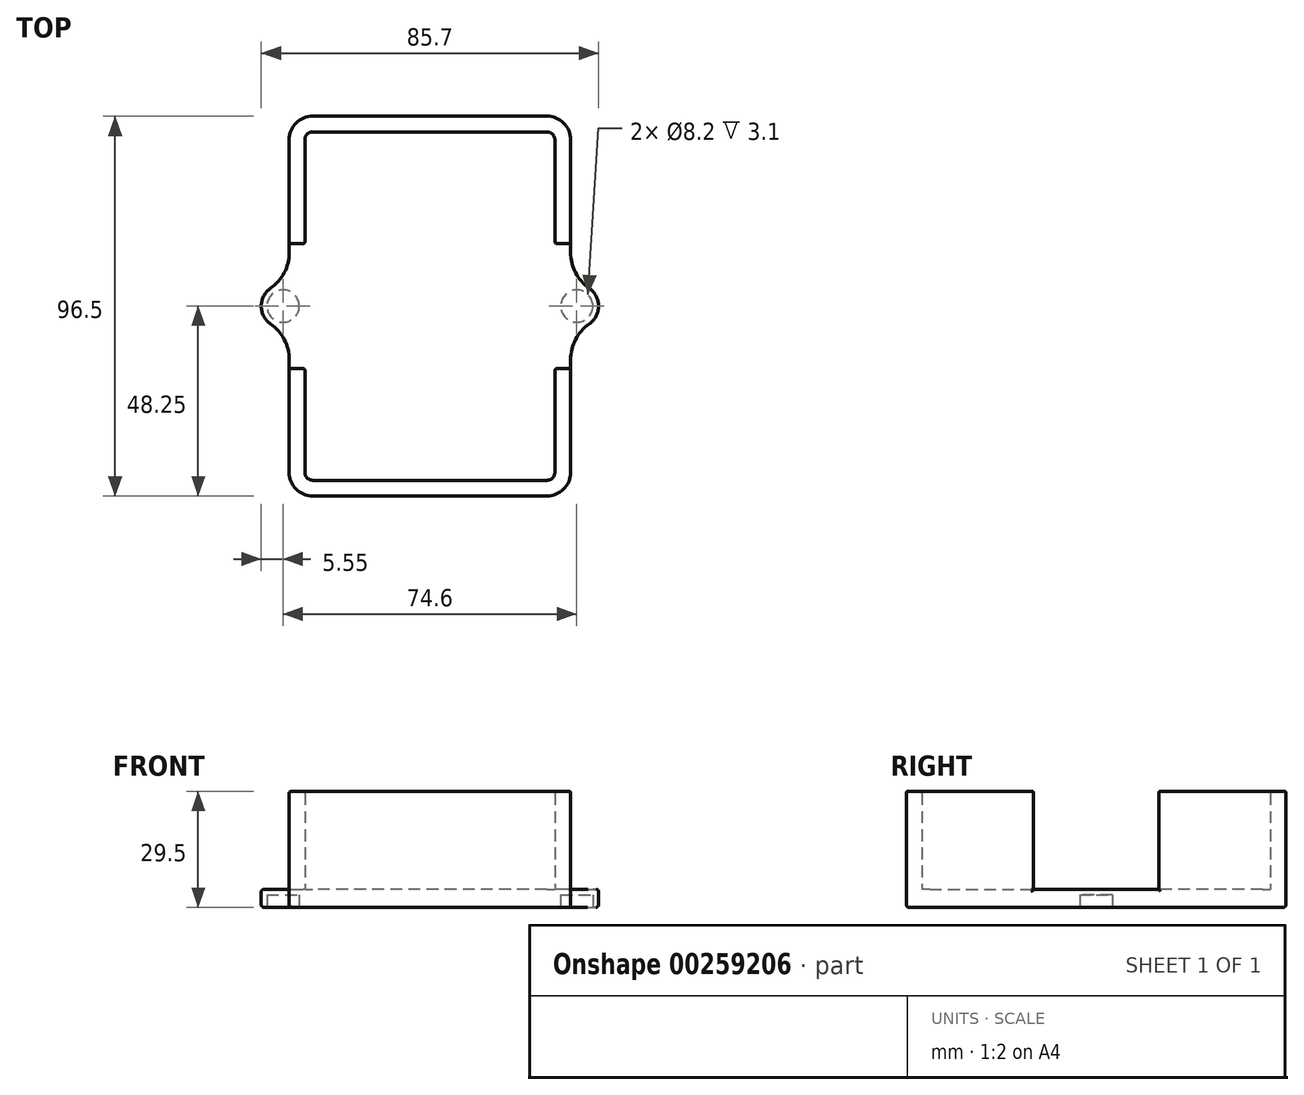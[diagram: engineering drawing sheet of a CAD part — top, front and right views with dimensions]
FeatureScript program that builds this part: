
annotation { "Feature Type Name" : "Feature", "Feature Type Description" : "" }
export const myFeature = defineFeature(function(context is Context, id is Id, definition is map)
    precondition{}
    {
        {
            var Q0;
            Q0=qCreatedBy(makeId("Top.planeOp"),FACE);
            var sketch = newSketch(context, id + "F0", { "sketchPlane" : qUnion([Q0])});
            skLineSegment(sketch, "E0", {"start": v(35.75, 42.25) * mm, "end": v(35.75, 13.59) * mm});
            skArc(sketch, "E1", {"start": v(35.75, 13.59) * mm, "mid": v(37, 8.5) * mm, "end": v(40.47, 4.56) * mm});
            skArc(sketch, "E2", {"start": v(40.47, 4.56) * mm, "mid": v(42.85, 0) * mm, "end": v(40.47, -4.56) * mm});
            skArc(sketch, "E3", {"start": v(40.47, -4.56) * mm, "mid": v(37, -8.5) * mm, "end": v(35.75, -13.59) * mm});
            skLineSegment(sketch, "E4", {"start": v(35.75, -13.59) * mm, "end": v(35.75, -42.25) * mm});
            skArc(sketch, "E5", {"start": v(35.75, -42.25) * mm, "mid": v(34, -46.5) * mm, "end": v(29.75, -48.25) * mm});
            skLineSegment(sketch, "E6", {"start": v(29.75, -48.25) * mm, "end": v(-29.75, -48.25) * mm});
            skArc(sketch, "E7", {"start": v(-29.75, -48.25) * mm, "mid": v(-34, -46.5) * mm, "end": v(-35.75, -42.25) * mm});
            skLineSegment(sketch, "E8", {"start": v(-35.75, -42.25) * mm, "end": v(-35.75, -13.59) * mm});
            skArc(sketch, "E9", {"start": v(-35.75, -13.59) * mm, "mid": v(-37, -8.5) * mm, "end": v(-40.47, -4.56) * mm});
            skArc(sketch, "E10", {"start": v(-40.47, -4.56) * mm, "mid": v(-42.85, 0) * mm, "end": v(-40.47, 4.56) * mm});
            skArc(sketch, "E11", {"start": v(-40.47, 4.56) * mm, "mid": v(-37, 8.5) * mm, "end": v(-35.75, 13.59) * mm});
            skLineSegment(sketch, "E12", {"start": v(-35.75, 13.59) * mm, "end": v(-35.75, 42.25) * mm});
            skArc(sketch, "E13", {"start": v(-35.75, 42.25) * mm, "mid": v(-34, 46.5) * mm, "end": v(-29.75, 48.25) * mm});
            skLineSegment(sketch, "E14", {"start": v(-29.75, 48.25) * mm, "end": v(29.75, 48.25) * mm});
            skArc(sketch, "E15", {"start": v(29.75, 48.25) * mm, "mid": v(34, 46.5) * mm, "end": v(35.75, 42.25) * mm});
            skSolve(sketch);
        }
        {
            var Q0;
            Q0 = qSketchRegion(id + "F0", true);
            extrude(context, id + "F1", {"entities" : qUnion([Q0]), "depth" : 4.5 * mm});
        }
        {
            var Q0;
            Q0=makeQuery(id+"F1.opExtrude","CAP_FACE",FACE,{"disambiguationData":[OSD([sQuery(id+"F0.wireOp",EDGE,"E0"),sQuery(id+"F0.wireOp",EDGE,"E1"),sQuery(id+"F0.wireOp",EDGE,"E2"),sQuery(id+"F0.wireOp",EDGE,"E3"),sQuery(id+"F0.wireOp",EDGE,"E4"),sQuery(id+"F0.wireOp",EDGE,"E5"),sQuery(id+"F0.wireOp",EDGE,"E6"),sQuery(id+"F0.wireOp",EDGE,"E7"),sQuery(id+"F0.wireOp",EDGE,"E8"),sQuery(id+"F0.wireOp",EDGE,"E9"),sQuery(id+"F0.wireOp",EDGE,"E10"),sQuery(id+"F0.wireOp",EDGE,"E11"),sQuery(id+"F0.wireOp",EDGE,"E12"),sQuery(id+"F0.wireOp",EDGE,"E13"),sQuery(id+"F0.wireOp",EDGE,"E14"),sQuery(id+"F0.wireOp",EDGE,"E15")])],"isStart":true});
            var sketch = newSketch(context, id + "F2", { "sketchPlane" : qUnion([Q0])});
            skCircle(sketch, "E16", {"center": v(-37.3, 0) * mm, "radius": 4.1 * mm});
            skCircle(sketch, "E17", {"center": v(37.3, 0) * mm, "radius": 4.1 * mm});
            skSolve(sketch);
        }
        {
            var Q0;
            Q0 = qSketchRegion(id + "F2", true);
            extrude(context, id + "F3", {"entities" : qUnion([Q0]), "operationType" : NewBodyOperationType.REMOVE, "oppositeDirection" : true, "depth" : 3.1 * mm});
        }
        {
            var Q0;
            Q0=makeQuery(id+"F1.opExtrude","CAP_FACE",FACE,{"disambiguationData":[OSD([sQuery(id+"F0.wireOp",EDGE,"E0"),sQuery(id+"F0.wireOp",EDGE,"E1"),sQuery(id+"F0.wireOp",EDGE,"E2"),sQuery(id+"F0.wireOp",EDGE,"E3"),sQuery(id+"F0.wireOp",EDGE,"E4"),sQuery(id+"F0.wireOp",EDGE,"E5"),sQuery(id+"F0.wireOp",EDGE,"E6"),sQuery(id+"F0.wireOp",EDGE,"E7"),sQuery(id+"F0.wireOp",EDGE,"E8"),sQuery(id+"F0.wireOp",EDGE,"E9"),sQuery(id+"F0.wireOp",EDGE,"E10"),sQuery(id+"F0.wireOp",EDGE,"E11"),sQuery(id+"F0.wireOp",EDGE,"E12"),sQuery(id+"F0.wireOp",EDGE,"E13"),sQuery(id+"F0.wireOp",EDGE,"E14"),sQuery(id+"F0.wireOp",EDGE,"E15")])],"isStart":false});
            var sketch = newSketch(context, id + "F4", { "sketchPlane" : qUnion([Q0])});
            skArc(sketch, "E18", {"start": v(-35.75, 16.39) * mm, "mid": v(-35.6, 16.03) * mm, "end": v(-35.25, 15.89) * mm});
            skLineSegment(sketch, "E19", {"start": v(-35.25, 15.89) * mm, "end": v(-32.25, 15.89) * mm});
            skArc(sketch, "E20", {"start": v(-32.25, 15.89) * mm, "mid": v(-31.9, 16.03) * mm, "end": v(-31.75, 16.39) * mm});
            skLineSegment(sketch, "E21", {"start": v(-31.75, 16.39) * mm, "end": v(-31.75, 42.25) * mm});
            skArc(sketch, "E22", {"start": v(-31.75, 42.25) * mm, "mid": v(-31.16, 43.66) * mm, "end": v(-29.75, 44.25) * mm});
            skLineSegment(sketch, "E23", {"start": v(-29.75, 44.25) * mm, "end": v(29.75, 44.25) * mm});
            skArc(sketch, "E24", {"start": v(29.75, 44.25) * mm, "mid": v(31.16, 43.66) * mm, "end": v(31.75, 42.25) * mm});
            skLineSegment(sketch, "E25", {"start": v(31.75, 42.25) * mm, "end": v(31.75, 16.39) * mm});
            skArc(sketch, "E26", {"start": v(31.75, 16.39) * mm, "mid": v(31.9, 16.03) * mm, "end": v(32.25, 15.89) * mm});
            skLineSegment(sketch, "E27", {"start": v(32.25, 15.89) * mm, "end": v(35.25, 15.89) * mm});
            skArc(sketch, "E28", {"start": v(35.25, 15.89) * mm, "mid": v(35.6, 16.03) * mm, "end": v(35.75, 16.39) * mm});
            skLineSegment(sketch, "E29", {"start": v(35.75, 16.39) * mm, "end": v(35.75, 42.25) * mm});
            skArc(sketch, "E30", {"start": v(35.75, 42.25) * mm, "mid": v(34, 46.5) * mm, "end": v(29.75, 48.25) * mm});
            skLineSegment(sketch, "E31", {"start": v(29.75, 48.25) * mm, "end": v(-29.75, 48.25) * mm});
            skArc(sketch, "E32", {"start": v(-29.75, 48.25) * mm, "mid": v(-34, 46.5) * mm, "end": v(-35.75, 42.25) * mm});
            skLineSegment(sketch, "E33", {"start": v(-35.75, 42.25) * mm, "end": v(-35.75, 16.39) * mm});
            skArc(sketch, "E34", {"start": v(35.75, -16.39) * mm, "mid": v(35.6, -16.03) * mm, "end": v(35.25, -15.89) * mm});
            skLineSegment(sketch, "E35", {"start": v(35.25, -15.89) * mm, "end": v(32.25, -15.89) * mm});
            skArc(sketch, "E36", {"start": v(32.25, -15.89) * mm, "mid": v(31.9, -16.03) * mm, "end": v(31.75, -16.39) * mm});
            skLineSegment(sketch, "E37", {"start": v(31.75, -16.39) * mm, "end": v(31.75, -42.25) * mm});
            skArc(sketch, "E38", {"start": v(31.75, -42.25) * mm, "mid": v(31.16, -43.66) * mm, "end": v(29.75, -44.25) * mm});
            skLineSegment(sketch, "E39", {"start": v(29.75, -44.25) * mm, "end": v(-29.75, -44.25) * mm});
            skArc(sketch, "E40", {"start": v(-29.75, -44.25) * mm, "mid": v(-31.16, -43.66) * mm, "end": v(-31.75, -42.25) * mm});
            skLineSegment(sketch, "E41", {"start": v(-31.75, -42.25) * mm, "end": v(-31.75, -16.39) * mm});
            skArc(sketch, "E42", {"start": v(-31.75, -16.39) * mm, "mid": v(-31.9, -16.03) * mm, "end": v(-32.25, -15.89) * mm});
            skLineSegment(sketch, "E43", {"start": v(-32.25, -15.89) * mm, "end": v(-35.25, -15.89) * mm});
            skArc(sketch, "E44", {"start": v(-35.25, -15.89) * mm, "mid": v(-35.6, -16.03) * mm, "end": v(-35.75, -16.39) * mm});
            skLineSegment(sketch, "E45", {"start": v(-35.75, -16.39) * mm, "end": v(-35.75, -42.25) * mm});
            skArc(sketch, "E46", {"start": v(-35.75, -42.25) * mm, "mid": v(-34, -46.5) * mm, "end": v(-29.75, -48.25) * mm});
            skLineSegment(sketch, "E47", {"start": v(-29.75, -48.25) * mm, "end": v(29.75, -48.25) * mm});
            skArc(sketch, "E48", {"start": v(29.75, -48.25) * mm, "mid": v(34, -46.5) * mm, "end": v(35.75, -42.25) * mm});
            skLineSegment(sketch, "E49", {"start": v(35.75, -42.25) * mm, "end": v(35.75, -16.39) * mm});
            skSolve(sketch);
        }
        {
            var Q0;
            Q0 = qSketchRegion(id + "F4", true);
            extrude(context, id + "F5", {"entities" : qUnion([Q0]), "operationType" : NewBodyOperationType.ADD, "depth" : 25 * mm});
        }
        {
            var Q0;
            Q0=makeQuery(id+"F1.opExtrude","CAP_EDGE",EDGE,{"disambiguationData":[OSD([sQuery(id+"F0.wireOp",EDGE,"E14")])],"isStart":true});
            var Q1;
            Q1=makeQuery(id+"F1.opExtrude","CAP_EDGE",EDGE,{"disambiguationData":[OSD([sQuery(id+"F0.wireOp",EDGE,"E13")])],"isStart":true});
            var Q2;
            Q2=makeQuery(id+"F1.opExtrude","CAP_EDGE",EDGE,{"disambiguationData":[OSD([sQuery(id+"F0.wireOp",EDGE,"E12")])],"isStart":true});
            var Q3;
            Q3=makeQuery(id+"F1.opExtrude","CAP_EDGE",EDGE,{"disambiguationData":[OSD([sQuery(id+"F0.wireOp",EDGE,"E11")])],"isStart":true});
            var Q4;
            Q4=makeQuery(id+"F1.opExtrude","CAP_EDGE",EDGE,{"disambiguationData":[OSD([sQuery(id+"F0.wireOp",EDGE,"E10")])],"isStart":true});
            var Q5;
            Q5=makeQuery(id+"F1.opExtrude","CAP_EDGE",EDGE,{"disambiguationData":[OSD([sQuery(id+"F0.wireOp",EDGE,"E9")])],"isStart":true});
            var Q6;
            Q6=makeQuery(id+"F1.opExtrude","CAP_EDGE",EDGE,{"disambiguationData":[OSD([sQuery(id+"F0.wireOp",EDGE,"E8")])],"isStart":true});
            var Q7;
            Q7=makeQuery(id+"F1.opExtrude","CAP_EDGE",EDGE,{"disambiguationData":[OSD([sQuery(id+"F0.wireOp",EDGE,"E7")])],"isStart":true});
            var Q8;
            Q8=makeQuery(id+"F1.opExtrude","CAP_EDGE",EDGE,{"disambiguationData":[OSD([sQuery(id+"F0.wireOp",EDGE,"E6")])],"isStart":true});
            var Q9;
            Q9=makeQuery(id+"F1.opExtrude","CAP_EDGE",EDGE,{"disambiguationData":[OSD([sQuery(id+"F0.wireOp",EDGE,"E5")])],"isStart":true});
            var Q10;
            Q10=makeQuery(id+"F1.opExtrude","CAP_EDGE",EDGE,{"disambiguationData":[OSD([sQuery(id+"F0.wireOp",EDGE,"E4")])],"isStart":true});
            var Q11;
            Q11=makeQuery(id+"F1.opExtrude","CAP_EDGE",EDGE,{"disambiguationData":[OSD([sQuery(id+"F0.wireOp",EDGE,"E3")])],"isStart":true});
            var Q12;
            Q12=makeQuery(id+"F1.opExtrude","CAP_EDGE",EDGE,{"disambiguationData":[OSD([sQuery(id+"F0.wireOp",EDGE,"E2")])],"isStart":true});
            var Q13;
            Q13=makeQuery(id+"F1.opExtrude","CAP_EDGE",EDGE,{"disambiguationData":[OSD([sQuery(id+"F0.wireOp",EDGE,"E1")])],"isStart":true});
            var Q14;
            Q14=makeQuery(id+"F1.opExtrude","CAP_EDGE",EDGE,{"disambiguationData":[OSD([sQuery(id+"F0.wireOp",EDGE,"E0")])],"isStart":true});
            var Q15;
            Q15=makeQuery(id+"F1.opExtrude","CAP_EDGE",EDGE,{"disambiguationData":[OSD([sQuery(id+"F0.wireOp",EDGE,"E15")])],"isStart":true});
            fillet(context, id + "F6", {"entities" : qUnion([Q0, Q1, Q2, Q3, Q4, Q5, Q6, Q7, Q8, Q9, Q10, Q11, Q12, Q13, Q14, Q15]), "radius" : .7 * mm, "tangentPropagation" : true, "allowEdgeOverflow" : false});
        }
        {
            var Q0;
            Q0=makeQuery(id+"F5.opExtrude","CAP_EDGE",EDGE,{"disambiguationData":[OSD([sQuery(id+"F4.wireOp",EDGE,"E43")])],"isStart":false});
            var Q1;
            Q1=makeQuery(id+"F5.opExtrude","CAP_EDGE",EDGE,{"disambiguationData":[OSD([sQuery(id+"F4.wireOp",EDGE,"E42")])],"isStart":false});
            var Q2;
            Q2=makeQuery(id+"F5.opExtrude","CAP_EDGE",EDGE,{"disambiguationData":[OSD([sQuery(id+"F4.wireOp",EDGE,"E41")])],"isStart":false});
            var Q3;
            Q3=makeQuery(id+"F5.opExtrude","CAP_EDGE",EDGE,{"disambiguationData":[OSD([sQuery(id+"F4.wireOp",EDGE,"E44")])],"isStart":false});
            var Q4;
            Q4=makeQuery(id+"F5.opExtrude","CAP_EDGE",EDGE,{"disambiguationData":[OSD([sQuery(id+"F4.wireOp",EDGE,"E45")])],"isStart":false});
            var Q5;
            Q5=makeQuery(id+"F5.opExtrude","CAP_EDGE",EDGE,{"disambiguationData":[OSD([sQuery(id+"F4.wireOp",EDGE,"E46")])],"isStart":false});
            var Q6;
            Q6=makeQuery(id+"F5.opExtrude","CAP_EDGE",EDGE,{"disambiguationData":[OSD([sQuery(id+"F4.wireOp",EDGE,"E40")])],"isStart":false});
            var Q7;
            Q7=makeQuery(id+"F5.opExtrude","CAP_EDGE",EDGE,{"disambiguationData":[OSD([sQuery(id+"F4.wireOp",EDGE,"E39")])],"isStart":false});
            var Q8;
            Q8=makeQuery(id+"F5.opExtrude","CAP_EDGE",EDGE,{"disambiguationData":[OSD([sQuery(id+"F4.wireOp",EDGE,"E47")])],"isStart":false});
            var Q9;
            Q9=makeQuery(id+"F5.opExtrude","CAP_EDGE",EDGE,{"disambiguationData":[OSD([sQuery(id+"F4.wireOp",EDGE,"E48")])],"isStart":false});
            var Q10;
            Q10=makeQuery(id+"F5.opExtrude","CAP_EDGE",EDGE,{"disambiguationData":[OSD([sQuery(id+"F4.wireOp",EDGE,"E38")])],"isStart":false});
            var Q11;
            Q11=makeQuery(id+"F5.opExtrude","CAP_EDGE",EDGE,{"disambiguationData":[OSD([sQuery(id+"F4.wireOp",EDGE,"E37")])],"isStart":false});
            var Q12;
            Q12=makeQuery(id+"F5.opExtrude","CAP_EDGE",EDGE,{"disambiguationData":[OSD([sQuery(id+"F4.wireOp",EDGE,"E49")])],"isStart":false});
            var Q13;
            Q13=makeQuery(id+"F5.opExtrude","CAP_EDGE",EDGE,{"disambiguationData":[OSD([sQuery(id+"F4.wireOp",EDGE,"E34")])],"isStart":false});
            var Q14;
            Q14=makeQuery(id+"F5.opExtrude","CAP_EDGE",EDGE,{"disambiguationData":[OSD([sQuery(id+"F4.wireOp",EDGE,"E35")])],"isStart":false});
            var Q15;
            Q15=makeQuery(id+"F5.opExtrude","CAP_EDGE",EDGE,{"disambiguationData":[OSD([sQuery(id+"F4.wireOp",EDGE,"E36")])],"isStart":false});
            var Q16;
            Q16=makeQuery(id+"F5.opExtrude","CAP_EDGE",EDGE,{"disambiguationData":[OSD([sQuery(id+"F4.wireOp",EDGE,"E27")])],"isStart":false});
            var Q17;
            Q17=makeQuery(id+"F5.opExtrude","CAP_EDGE",EDGE,{"disambiguationData":[OSD([sQuery(id+"F4.wireOp",EDGE,"E26")])],"isStart":false});
            var Q18;
            Q18=makeQuery(id+"F5.opExtrude","CAP_EDGE",EDGE,{"disambiguationData":[OSD([sQuery(id+"F4.wireOp",EDGE,"E25")])],"isStart":false});
            var Q19;
            Q19=makeQuery(id+"F5.opExtrude","CAP_EDGE",EDGE,{"disambiguationData":[OSD([sQuery(id+"F4.wireOp",EDGE,"E28")])],"isStart":false});
            var Q20;
            Q20=makeQuery(id+"F5.opExtrude","CAP_EDGE",EDGE,{"disambiguationData":[OSD([sQuery(id+"F4.wireOp",EDGE,"E29")])],"isStart":false});
            var Q21;
            Q21=makeQuery(id+"F5.opExtrude","CAP_EDGE",EDGE,{"disambiguationData":[OSD([sQuery(id+"F4.wireOp",EDGE,"E30")])],"isStart":false});
            var Q22;
            Q22=makeQuery(id+"F5.opExtrude","CAP_EDGE",EDGE,{"disambiguationData":[OSD([sQuery(id+"F4.wireOp",EDGE,"E24")])],"isStart":false});
            var Q23;
            Q23=makeQuery(id+"F5.opExtrude","CAP_EDGE",EDGE,{"disambiguationData":[OSD([sQuery(id+"F4.wireOp",EDGE,"E23")])],"isStart":false});
            var Q24;
            Q24=makeQuery(id+"F5.opExtrude","CAP_EDGE",EDGE,{"disambiguationData":[OSD([sQuery(id+"F4.wireOp",EDGE,"E31")])],"isStart":false});
            var Q25;
            Q25=makeQuery(id+"F5.opExtrude","CAP_EDGE",EDGE,{"disambiguationData":[OSD([sQuery(id+"F4.wireOp",EDGE,"E22")])],"isStart":false});
            var Q26;
            Q26=makeQuery(id+"F5.opExtrude","CAP_EDGE",EDGE,{"disambiguationData":[OSD([sQuery(id+"F4.wireOp",EDGE,"E32")])],"isStart":false});
            var Q27;
            Q27=makeQuery(id+"F5.opExtrude","CAP_EDGE",EDGE,{"disambiguationData":[OSD([sQuery(id+"F4.wireOp",EDGE,"E33")])],"isStart":false});
            var Q28;
            Q28=makeQuery(id+"F5.opExtrude","CAP_EDGE",EDGE,{"disambiguationData":[OSD([sQuery(id+"F4.wireOp",EDGE,"E21")])],"isStart":false});
            var Q29;
            Q29=makeQuery(id+"F5.opExtrude","CAP_EDGE",EDGE,{"disambiguationData":[OSD([sQuery(id+"F4.wireOp",EDGE,"E20")])],"isStart":false});
            var Q30;
            Q30=makeQuery(id+"F5.opExtrude","CAP_EDGE",EDGE,{"disambiguationData":[OSD([sQuery(id+"F4.wireOp",EDGE,"E19")])],"isStart":false});
            var Q31;
            Q31=makeQuery(id+"F5.opExtrude","CAP_EDGE",EDGE,{"disambiguationData":[OSD([sQuery(id+"F4.wireOp",EDGE,"E18")])],"isStart":false});
            fillet(context, id + "F7", {"entities" : qUnion([Q0, Q1, Q2, Q3, Q4, Q5, Q6, Q7, Q8, Q9, Q10, Q11, Q12, Q13, Q14, Q15, Q16, Q17, Q18, Q19, Q20, Q21, Q22, Q23, Q24, Q25, Q26, Q27, Q28, Q29, Q30, Q31]), "radius" : .5 * mm, "tangentPropagation" : true, "allowEdgeOverflow" : false});
        }
        {
            var Q0;
            Q0=makeQuery(id+"F1.opExtrude","CAP_EDGE",EDGE,{"disambiguationData":[OSD([sQuery(id+"F0.wireOp",EDGE,"E3")])],"isStart":false});
            var Q1;
            Q1=makeQuery(id+"F1.opExtrude","CAP_EDGE",EDGE,{"disambiguationData":[OSD([sQuery(id+"F0.wireOp",EDGE,"E2")])],"isStart":false});
            var Q2;
            Q2=makeQuery(id+"F1.opExtrude","CAP_EDGE",EDGE,{"disambiguationData":[OSD([sQuery(id+"F0.wireOp",EDGE,"E1")])],"isStart":false});
            var Q3;
            Q3=makeQuery(id+"F1.opExtrude","CAP_EDGE",EDGE,{"disambiguationData":[OSD([sQuery(id+"F0.wireOp",EDGE,"E4")])],"isStart":false});
            var Q4;
            Q4=makeQuery(id+"F1.opExtrude","CAP_EDGE",EDGE,{"disambiguationData":[OSD([sQuery(id+"F0.wireOp",EDGE,"E0")])],"isStart":false});
            fillet(context, id + "F8", {"entities" : qUnion([Q0, Q1, Q2, Q3, Q4]), "radius" : .5 * mm, "tangentPropagation" : true, "allowEdgeOverflow" : false});
        }
        {
            var Q0;
            Q0=makeQuery(id+"F1.opExtrude","CAP_EDGE",EDGE,{"disambiguationData":[OSD([sQuery(id+"F0.wireOp",EDGE,"E8")])],"isStart":false});
            var Q1;
            Q1=makeQuery(id+"F1.opExtrude","CAP_EDGE",EDGE,{"disambiguationData":[OSD([sQuery(id+"F0.wireOp",EDGE,"E9")])],"isStart":false});
            var Q2;
            Q2=makeQuery(id+"F1.opExtrude","CAP_EDGE",EDGE,{"disambiguationData":[OSD([sQuery(id+"F0.wireOp",EDGE,"E10")])],"isStart":false});
            var Q3;
            Q3=makeQuery(id+"F1.opExtrude","CAP_EDGE",EDGE,{"disambiguationData":[OSD([sQuery(id+"F0.wireOp",EDGE,"E12")])],"isStart":false});
            var Q4;
            Q4=makeQuery(id+"F1.opExtrude","CAP_EDGE",EDGE,{"disambiguationData":[OSD([sQuery(id+"F0.wireOp",EDGE,"E11")])],"isStart":false});
            fillet(context, id + "F9", {"entities" : qUnion([Q0, Q1, Q2, Q3, Q4]), "radius" : .5 * mm, "tangentPropagation" : true, "allowEdgeOverflow" : false});
        }
        {
            var Q0;
            Q0=makeQuery(id+"F1.opExtrude","CAP_FACE",FACE,{"disambiguationData":[OSD([sQuery(id+"F0.wireOp",EDGE,"E0"),sQuery(id+"F0.wireOp",EDGE,"E1"),sQuery(id+"F0.wireOp",EDGE,"E2"),sQuery(id+"F0.wireOp",EDGE,"E3"),sQuery(id+"F0.wireOp",EDGE,"E4"),sQuery(id+"F0.wireOp",EDGE,"E5"),sQuery(id+"F0.wireOp",EDGE,"E6"),sQuery(id+"F0.wireOp",EDGE,"E7"),sQuery(id+"F0.wireOp",EDGE,"E8"),sQuery(id+"F0.wireOp",EDGE,"E9"),sQuery(id+"F0.wireOp",EDGE,"E10"),sQuery(id+"F0.wireOp",EDGE,"E11"),sQuery(id+"F0.wireOp",EDGE,"E12"),sQuery(id+"F0.wireOp",EDGE,"E13"),sQuery(id+"F0.wireOp",EDGE,"E14"),sQuery(id+"F0.wireOp",EDGE,"E15")])],"isStart":false});
            var sketch = newSketch(context, id + "F10", { "sketchPlane" : qUnion([Q0])});
            skCircle(sketch, "E50", {"center": v(0, 0) * mm, "radius": 10.19 * mm});
            skSolve(sketch);
        }
        {
            var Q0;
            Q0=makeQuery(id+"F10.imprint","IMPRINT",FACE,{"disambiguationData":[TD([[makeQuery(id+"F10.imprint","IMPRINT",EDGE,{"derivedFrom":sQuery(id+"F10.wireOp",EDGE,"E50")}),1.0]])]});
            var Q1;
            Q1=sQuery(id+"F10.wireOp",EDGE,"E50");
            extrude(context, id + "F11", {"entities" : qUnion([Q0]), "operationType" : NewBodyOperationType.REMOVE, "surfaceEntities" : qUnion([Q1]), "depth" : 25 * mm});
        }
    });
